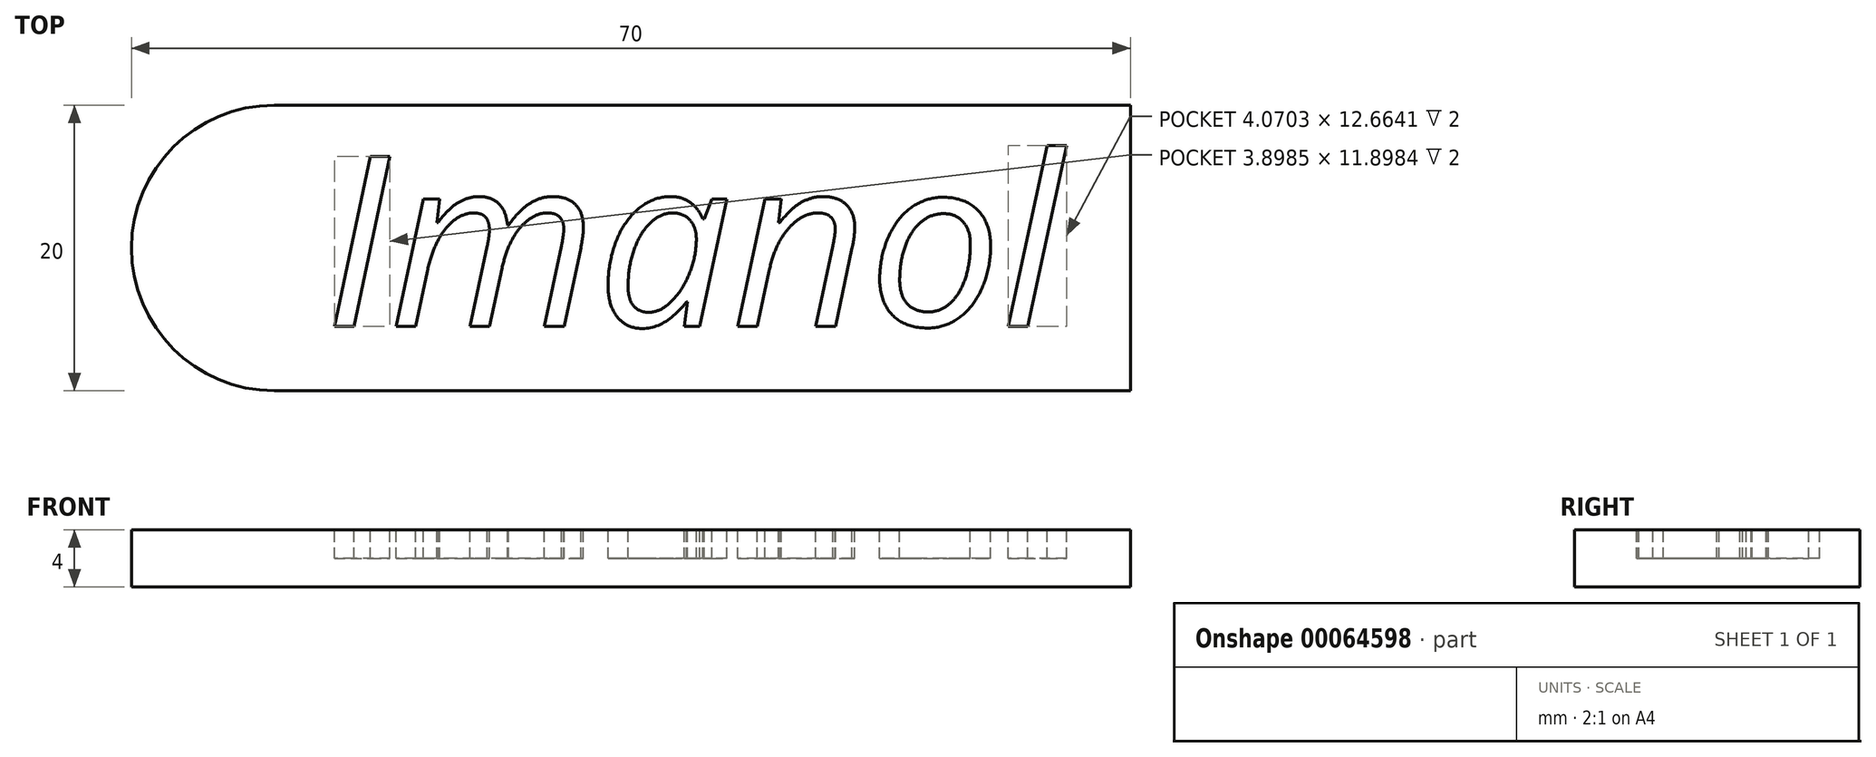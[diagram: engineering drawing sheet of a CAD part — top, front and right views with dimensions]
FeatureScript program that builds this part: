
annotation { "Feature Type Name" : "Feature", "Feature Type Description" : "" }
export const myFeature = defineFeature(function(context is Context, id is Id, definition is map)
    precondition{}
    {
        {
            var Q0;
            Q0=qCreatedBy(makeId("Top.planeOp"),FACE);
            var sketch = newSketch(context, id + "F0", { "sketchPlane" : qUnion([Q0])});
            skLineSegment(sketch, "E0.rect.bottom", {"start": v(30, 10) * mm, "end": v(-30, 10) * mm});
            skLineSegment(sketch, "E0.rect.top", {"start": v(30, -10) * mm, "end": v(-30, -10) * mm});
            skLineSegment(sketch, "E0.rect.left", {"start": v(30, 10) * mm, "end": v(30, -10) * mm});
            skPoint(sketch, "E0.rect.middle", {"position": v(0, 0) * mm});
            skArc(sketch, "E1", {"start": v(-30, 10) * mm, "mid": v(-40, 0) * mm, "end": v(-30, -10) * mm});
            skSolve(sketch);
        }
        {
            var Q0;
            Q0 = qSketchRegion(id + "F0", true);
            extrude(context, id + "F1", {"entities" : qUnion([Q0]), "depth" : 4 * mm});
        }
        {
            var Q0;
            Q0=makeQuery(id+"F1.opExtrude","CAP_FACE",FACE,{"disambiguationData":[OSD([sQuery(id+"F0.wireOp",EDGE,"E0.rect.bottom"),sQuery(id+"F0.wireOp",EDGE,"E0.rect.top"),sQuery(id+"F0.wireOp",EDGE,"E0.rect.left"),sQuery(id+"F0.wireOp",EDGE,"E1")])],"isStart":false});
            var sketch = newSketch(context, id + "F2", { "sketchPlane" : qUnion([Q0])});
            skText(sketch, "E2", { "text": "Imanol", "fontName": "OpenSans-Italic.ttf"});
            const initialGuessF2  = {"E2": [-0.02648, -0.00548, 1, 0, 0.012]};
            skSetInitialGuess(sketch, initialGuessF2);
            skSolve(sketch);
        }
        {
            var Q0;
            Q0 = qSketchRegion(id + "F2", true);
            extrude(context, id + "F3", {"entities" : qUnion([Q0]), "operationType" : NewBodyOperationType.REMOVE, "oppositeDirection" : true, "depth" : 2 * mm});
        }
    });
